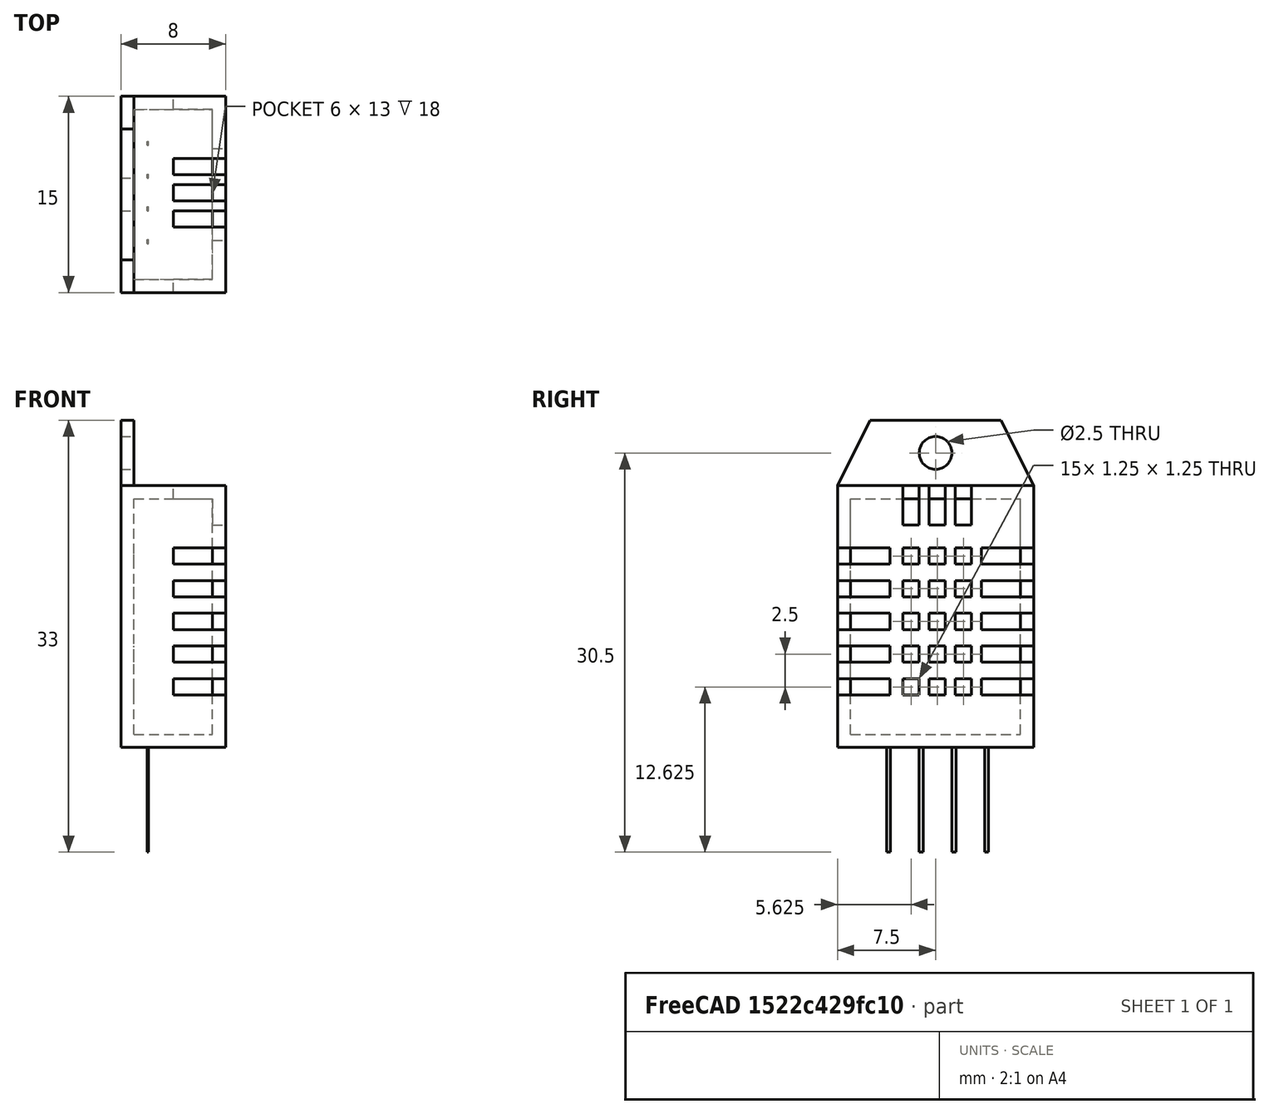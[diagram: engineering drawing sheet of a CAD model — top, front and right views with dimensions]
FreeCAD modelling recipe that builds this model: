
FCSTD DOCUMENT  (FreeCAD 0.16R)
Label: DHT22
License: All rights reserved
LicenseURL: http://en.wikipedia.org/wiki/All_rights_reserved
objects: Part::Box×35, Part::Cut×32, Part::Wedge×2, Part::Cylinder×1
note: 70 computed .brp shape members not serialized (recipe doc carries the construction recipe); baked Part::Feature solids carry a one-line shape summary decoded from their .brp

FEATURE [Part::Box] Box  label="Cube"
  Height = 20
  Length = 8
  Placement = pos=(0,0,1) rot=(0,0,1;0rad)
  Width = 15
FEATURE [Part::Box] Box001  label="Cube001"
  Height = 1.25
  Length = 7
  Placement = pos=(1,5,15) rot=(0,0,1;0rad)
  Width = 1.25
FEATURE [Part::Box] Box002  label="Cube002"
  Height = 1.25
  Length = 7
  Placement = pos=(1,7,15) rot=(0,0,1;0rad)
  Width = 1.25
FEATURE [Part::Box] Box003  label="Cube003"
  Height = 1.25
  Length = 7
  Placement = pos=(1,9,15) rot=(0,0,1;0rad)
  Width = 1.25
FEATURE [Part::Box] Box004  label="Cube004"
  Height = 1.25
  Length = 7
  Placement = pos=(1,7,12.5) rot=(0,0,1;0rad)
  Width = 1.25
FEATURE [Part::Box] Box005  label="Cube005"
  Height = 1.25
  Length = 7
  Placement = pos=(1,9,12.5) rot=(0,0,1;0rad)
  Width = 1.25
FEATURE [Part::Box] Box006  label="Cube006"
  Height = 1.25
  Length = 7
  Placement = pos=(1,5,12.5) rot=(0,0,1;0rad)
  Width = 1.25
FEATURE [Part::Box] Box007  label="Cube007"
  Height = 1.25
  Length = 7
  Placement = pos=(1,5,10) rot=(0,0,1;0rad)
  Width = 1.25
FEATURE [Part::Box] Box008  label="Cube008"
  Height = 1.25
  Length = 7
  Placement = pos=(1,9,10) rot=(0,0,1;0rad)
  Width = 1.25
FEATURE [Part::Box] Box009  label="Cube009"
  Height = 1.25
  Length = 7
  Placement = pos=(1,9,7.5) rot=(0,0,1;0rad)
  Width = 1.25
FEATURE [Part::Box] Box010  label="Cube010"
  Height = 1.25
  Length = 7
  Placement = pos=(1,7,10) rot=(0,0,1;0rad)
  Width = 1.25
FEATURE [Part::Box] Box011  label="Cube011"
  Height = 1.25
  Length = 7
  Placement = pos=(1,7,7.5) rot=(0,0,1;0rad)
  Width = 1.25
FEATURE [Part::Box] Box012  label="Cube012"
  Height = 1.25
  Length = 7
  Placement = pos=(1,5,7.5) rot=(0,0,1;0rad)
  Width = 1.25
FEATURE [Part::Box] Box013  label="Cube013"
  Height = 1.25
  Length = 7
  Placement = pos=(1,5,5) rot=(0,0,1;0rad)
  Width = 1.25
FEATURE [Part::Box] Box014  label="Cube014"
  Height = 1.25
  Length = 7
  Placement = pos=(1,7,5) rot=(0,0,1;0rad)
  Width = 1.25
FEATURE [Part::Box] Box015  label="Cube015"
  Height = 1.25
  Length = 7
  Placement = pos=(1,9,5) rot=(0,0,1;0rad)
  Width = 1.25
FEATURE [Part::Box] Box016  label="Cube016"
  Height = 1.25
  Length = 4
  Placement = pos=(4,0,5) rot=(0,0,1;0rad)
  Width = 4
FEATURE [Part::Box] Box017  label="Cube017"
  Height = 1.25
  Length = 4
  Placement = pos=(4,0,7.5) rot=(0,0,1;0rad)
  Width = 4
FEATURE [Part::Box] Box018  label="Cube018"
  Height = 1.25
  Length = 4
  Placement = pos=(4,0,10) rot=(0,0,1;0rad)
  Width = 4
FEATURE [Part::Box] Box019  label="Cube019"
  Height = 1.25
  Length = 4
  Placement = pos=(4,0,12.5) rot=(0,0,1;0rad)
  Width = 4
FEATURE [Part::Box] Box020  label="Cube020"
  Height = 1.25
  Length = 4
  Placement = pos=(4,0,15) rot=(0,0,1;0rad)
  Width = 4
FEATURE [Part::Box] Box021  label="Cube021"
  Height = 1.25
  Length = 4
  Placement = pos=(4,11,15) rot=(0,0,1;0rad)
  Width = 4
FEATURE [Part::Box] Box022  label="Cube022"
  Height = 1.25
  Length = 4
  Placement = pos=(4,11,12.5) rot=(0,0,1;0rad)
  Width = 4
FEATURE [Part::Box] Box023  label="Cube023"
  Height = 1.25
  Length = 4
  Placement = pos=(4,11,10) rot=(0,0,1;0rad)
  Width = 4
FEATURE [Part::Box] Box024  label="Cube024"
  Height = 1.25
  Length = 4
  Placement = pos=(4,11,7.5) rot=(0,0,1;0rad)
  Width = 4
FEATURE [Part::Box] Box025  label="Cube025"
  Height = 1.25
  Length = 4
  Placement = pos=(4,11,5) rot=(0,0,1;0rad)
  Width = 4
FEATURE [Part::Box] Box026  label="Cube026"
  Height = 3
  Length = 4
  Placement = pos=(4,9,18) rot=(0,0,1;0rad)
  Width = 1.25
FEATURE [Part::Box] Box027  label="Cube027"
  Height = 3
  Length = 4
  Placement = pos=(4,7,18) rot=(0,0,1;0rad)
  Width = 1.25
FEATURE [Part::Box] Box028  label="Cube028"
  Height = 3
  Length = 4
  Placement = pos=(4,5,18) rot=(0,0,1;0rad)
  Width = 1.25
FEATURE [Part::Box] Box029  label="Middle"
  Height = 18
  Length = 6
  Placement = pos=(1,1,2) rot=(0,0,1;0rad)
  Width = 13
FEATURE [Part::Cut] Cut
  Base = -> Box
  Tool = -> Box001
FEATURE [Part::Cut] Cut001
  Base = -> Cut
  Tool = -> Box002
FEATURE [Part::Cut] Cut002
  Base = -> Cut001
  Tool = -> Box003
FEATURE [Part::Cut] Cut003
  Base = -> Cut002
  Tool = -> Box004
FEATURE [Part::Cut] Cut004
  Base = -> Cut003
  Tool = -> Box005
FEATURE [Part::Cut] Cut005
  Base = -> Cut004
  Tool = -> Box006
FEATURE [Part::Cut] Cut006
  Base = -> Cut005
  Tool = -> Box007
FEATURE [Part::Cut] Cut007
  Base = -> Cut006
  Tool = -> Box008
FEATURE [Part::Cut] Cut008
  Base = -> Cut007
  Tool = -> Box009
FEATURE [Part::Cut] Cut009
  Base = -> Cut008
  Tool = -> Box010
FEATURE [Part::Cut] Cut010
  Base = -> Cut009
  Tool = -> Box011
FEATURE [Part::Cut] Cut011
  Base = -> Cut010
  Tool = -> Box012
FEATURE [Part::Cut] Cut012
  Base = -> Cut011
  Tool = -> Box013
FEATURE [Part::Wedge] Wedge  label="Prisme"
  Placement = pos=(0,0,26) rot=(-1,0,0;1.5708rad)
  X2max = 1
  X2min = 0
  Xmax = 1
  Xmin = 0
  Ymax = 5
  Ymin = 0
  Z2max = 0
  Z2min = 0
  Zmax = 2.5
  Zmin = 0
FEATURE [Part::Box] Box030  label="Cube029"
  Height = 5
  Length = 1
  Placement = pos=(0,0,21) rot=(0,0,1;0rad)
  Width = 15
FEATURE [Part::Wedge] Wedge001  label="Prisme001"
  Placement = pos=(0,15,26) rot=(1,0,0;3.14159rad)
  X2max = 1
  X2min = 0
  Xmax = 1
  Xmin = 0
  Ymax = 2.5
  Ymin = 0
  Z2max = 0
  Z2min = 0
  Zmax = 5
  Zmin = 0
FEATURE [Part::Cylinder] Cylinder  label="Cylindre"
  Angle = 360
  Height = 1
  Placement = pos=(0,7.5,23.5) rot=(0,1,0;1.5708rad)
  Radius = 1.25
FEATURE [Part::Box] Box031  label="Cube030"
  Height = 8
  Length = 0.1
  Placement = pos=(2,3.75,-7) rot=(0,0,1;0rad)
  Width = 0.3
FEATURE [Part::Cut] Cut029
  Base = -> Box030
  Tool = -> Wedge
FEATURE [Part::Cut] Cut030
  Base = -> Cut029
  Tool = -> Wedge001
FEATURE [Part::Cut] Cut031
  Base = -> Cut030
  Tool = -> Cylinder
FEATURE [Part::Box] Box032  label="Cube031"
  Height = 8
  Length = 0.1
  Placement = pos=(2,11.25,-7) rot=(0,0,1;0rad)
  Width = 0.3
FEATURE [Part::Box] Box033  label="Cube032"
  Height = 8
  Length = 0.1
  Placement = pos=(2,6.25,-7) rot=(0,0,1;0rad)
  Width = 0.3
FEATURE [Part::Box] Box034  label="Cube033"
  Height = 8
  Length = 0.1
  Placement = pos=(2,8.75,-7) rot=(0,0,1;0rad)
  Width = 0.3
FEATURE [Part::Cut] Cut013
  Base = -> Cut012
  Tool = -> Box014
FEATURE [Part::Cut] Cut014
  Base = -> Cut013
  Tool = -> Box015
FEATURE [Part::Cut] Cut032
  Base = -> Cut014
  Tool = -> Box016
FEATURE [Part::Cut] Cut033
  Base = -> Cut032
  Tool = -> Box017
FEATURE [Part::Cut] Cut034
  Base = -> Cut033
  Tool = -> Box018
FEATURE [Part::Cut] Cut035
  Base = -> Cut034
  Tool = -> Box019
FEATURE [Part::Cut] Cut036
  Base = -> Cut035
  Tool = -> Box020
FEATURE [Part::Cut] Cut037
  Base = -> Cut036
  Tool = -> Box021
FEATURE [Part::Cut] Cut038
  Base = -> Cut037
  Tool = -> Box022
FEATURE [Part::Cut] Cut039
  Base = -> Cut038
  Tool = -> Box023
FEATURE [Part::Cut] Cut040
  Base = -> Cut039
  Tool = -> Box024
FEATURE [Part::Cut] Cut041
  Base = -> Cut040
  Tool = -> Box025
FEATURE [Part::Cut] Cut042
  Base = -> Cut041
  Tool = -> Box028
FEATURE [Part::Cut] Cut043
  Base = -> Cut042
  Tool = -> Box026
FEATURE [Part::Cut] Cut044
  Base = -> Cut043
  Tool = -> Box027
FEATURE [Part::Cut] Cut045
  Base = -> Cut044
  Tool = -> Box029
